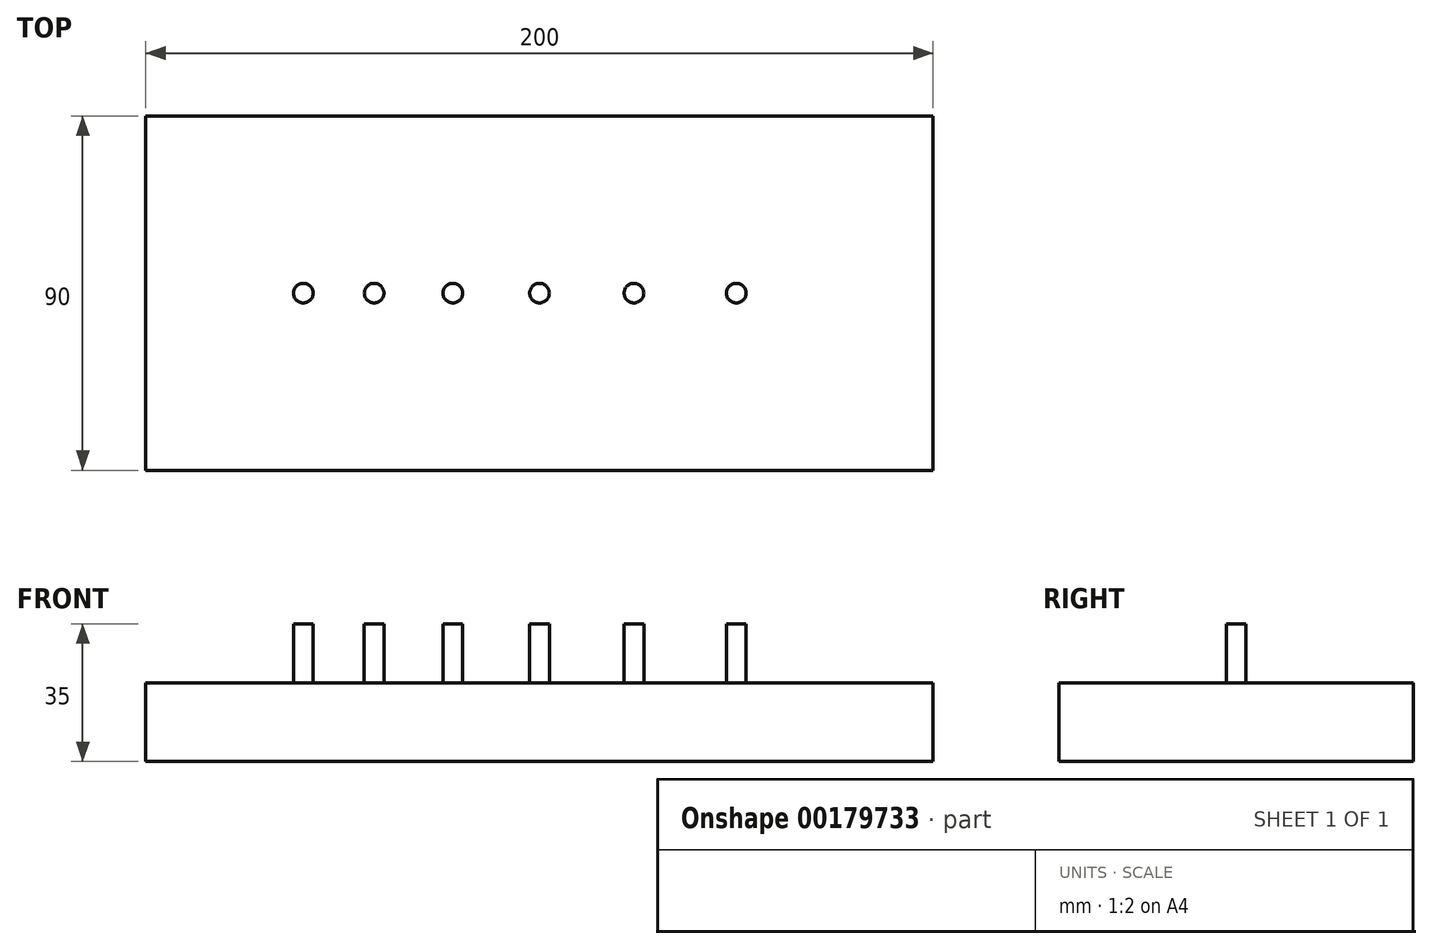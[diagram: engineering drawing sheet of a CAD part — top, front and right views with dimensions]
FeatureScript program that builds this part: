
annotation { "Feature Type Name" : "Feature", "Feature Type Description" : "" }
export const myFeature = defineFeature(function(context is Context, id is Id, definition is map)
    precondition{}
    {
        {
            var Q0;
            Q0=qCreatedBy(makeId("Top.planeOp"),FACE);
            var sketch = newSketch(context, id + "F0", { "sketchPlane" : qUnion([Q0])});
            skLineSegment(sketch, "E0.bottom", {"start": v(-100, 45) * mm, "end": v(100, 45) * mm});
            skLineSegment(sketch, "E0.top", {"start": v(-100, -45) * mm, "end": v(100, -45) * mm});
            skLineSegment(sketch, "E0.left", {"start": v(-100, 45) * mm, "end": v(-100, -45) * mm});
            skLineSegment(sketch, "E0.right", {"start": v(100, 45) * mm, "end": v(100, -45) * mm});
            skSolve(sketch);
        }
        {
            var Q0;
            Q0=makeQuery(id+"F0.imprint","IMPRINT",FACE,{"disambiguationData":[TD([[makeQuery(id+"F0.imprint","IMPRINT",EDGE,{"derivedFrom":sQuery(id+"F0.wireOp",EDGE,"E0.bottom")}),-1.0]])]});
            extrude(context, id + "F1", {"entities" : qUnion([Q0]), "depth" : 20 * mm});
        }
        {
            var Q0;
            Q0=makeQuery(id+"F1.opExtrude","CAP_FACE",FACE,{"disambiguationData":[OSD([sQuery(id+"F0.wireOp",EDGE,"E0.bottom"),sQuery(id+"F0.wireOp",EDGE,"E0.top"),sQuery(id+"F0.wireOp",EDGE,"E0.left"),sQuery(id+"F0.wireOp",EDGE,"E0.right")])],"isStart":false});
            var sketch = newSketch(context, id + "F2", { "sketchPlane" : qUnion([Q0])});
            skCircle(sketch, "E1", {"center": v(-60, 0) * mm, "radius": 2.5 * mm});
            skCircle(sketch, "E2", {"center": v(-42, 0) * mm, "radius": 2.5 * mm});
            skCircle(sketch, "E3", {"center": v(-22, 0) * mm, "radius": 2.5 * mm});
            skCircle(sketch, "E4", {"center": v(0, 0) * mm, "radius": 2.5 * mm});
            skCircle(sketch, "E5", {"center": v(24, 0) * mm, "radius": 2.5 * mm});
            skCircle(sketch, "E6", {"center": v(50, 0) * mm, "radius": 2.5 * mm});
            skSolve(sketch);
        }
        {
            var Q0;
            Q0 = qSketchRegion(id + "F2", true);
            extrude(context, id + "F3", {"entities" : qUnion([Q0]), "operationType" : NewBodyOperationType.ADD, "depth" : 15 * mm});
        }
    });
